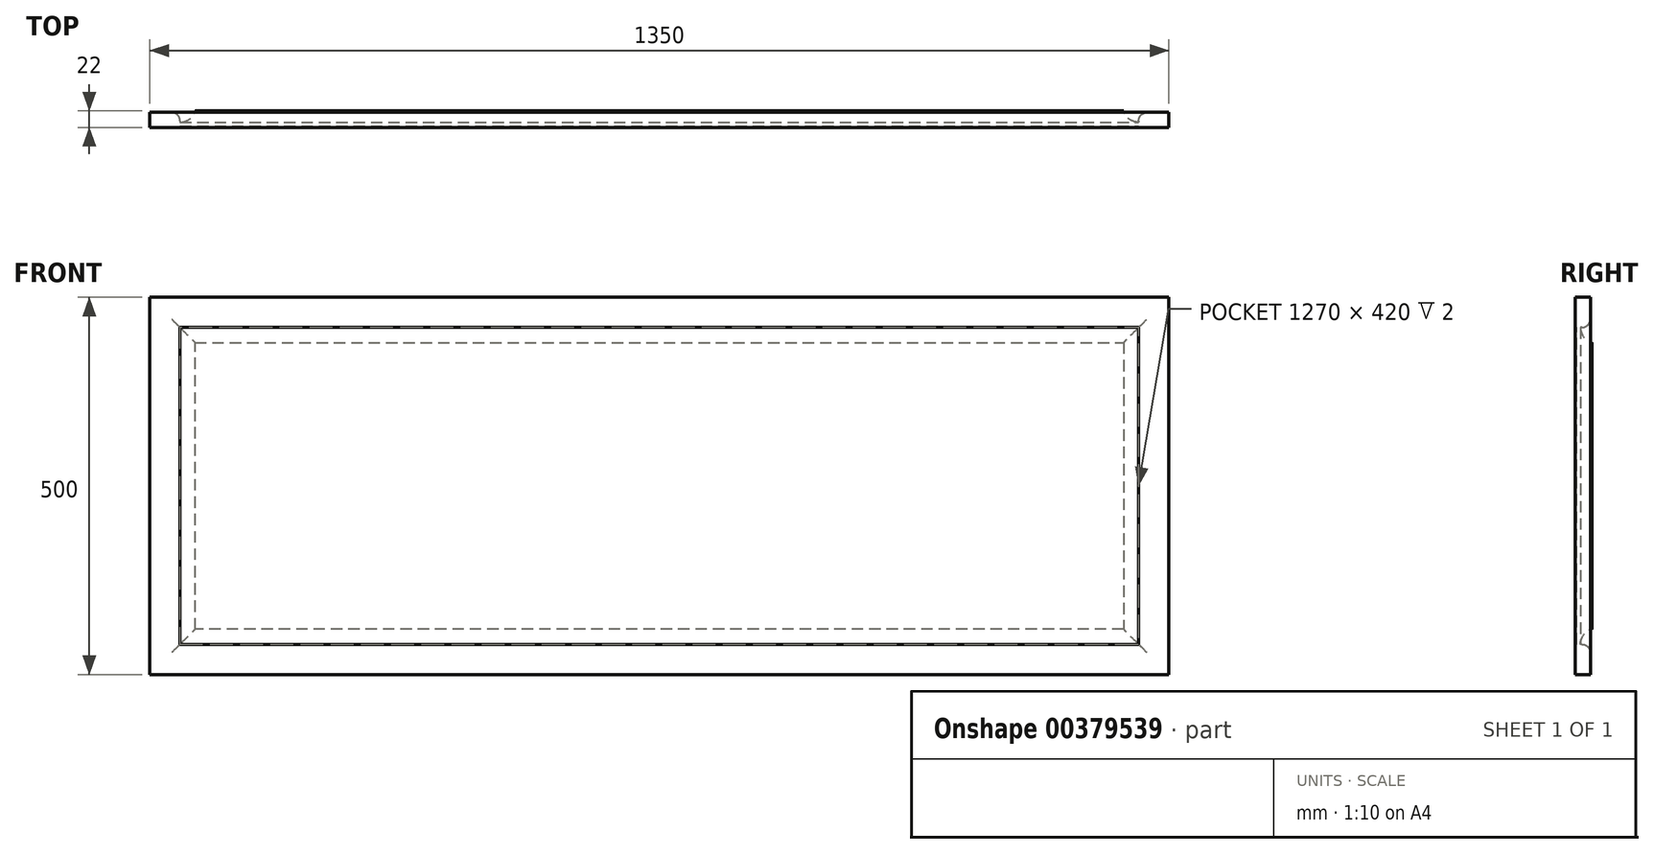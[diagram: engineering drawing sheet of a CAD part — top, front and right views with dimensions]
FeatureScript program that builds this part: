
annotation { "Feature Type Name" : "Feature", "Feature Type Description" : "" }
export const myFeature = defineFeature(function(context is Context, id is Id, definition is map)
    precondition{}
    {
        {
            var Q0;
            Q0=qCreatedBy(makeId("Front.planeOp"),FACE);
            var sketch = newSketch(context, id + "F0", { "sketchPlane" : qUnion([Q0])});
            skLineSegment(sketch, "E0.bottom", {"start": v(-675, 250) * mm, "end": v(675, 250) * mm});
            skLineSegment(sketch, "E0.top", {"start": v(-675, -250) * mm, "end": v(675, -250) * mm});
            skLineSegment(sketch, "E0.left", {"start": v(-675, 250) * mm, "end": v(-675, -250) * mm});
            skLineSegment(sketch, "E0.right", {"start": v(675, 250) * mm, "end": v(675, -250) * mm});
            skPoint(sketch, "E0.middle", {"position": v(0, 0) * mm});
            skLineSegment(sketch, "E1", {"start": v(-675, 250) * mm, "end": v(-225, 250) * mm, "construction": true});
            skLineSegment(sketch, "E2", {"start": v(-225, 250) * mm, "end": v(225, 250) * mm, "construction": true});
            skLineSegment(sketch, "E3", {"start": v(225, 250) * mm, "end": v(675, 250) * mm, "construction": true});
            skLineSegment(sketch, "E4", {"start": v(-225, 250) * mm, "end": v(-225, -250) * mm});
            skLineSegment(sketch, "E5", {"start": v(225, 250) * mm, "end": v(225, -250) * mm});
            skSolve(sketch);
        }
        {
            var Q0;
            Q0=qCreatedBy(makeId("Top.planeOp"),FACE);
            var sketch = newSketch(context, id + "F1", { "sketchPlane" : qUnion([Q0])});
            skLineSegment(sketch, "E6", {"start": v(0, 0) * mm, "end": v(-675, 0) * mm, "construction": true});
            skLineSegment(sketch, "E7", {"start": v(0, 0) * mm, "end": v(675, 0) * mm});
            skLineSegment(sketch, "E8", {"start": v(-675, 0) * mm, "end": v(-675, -7) * mm});
            skLineSegment(sketch, "E9", {"start": v(-675, -7) * mm, "end": v(-635, -7) * mm});
            skLineSegment(sketch, "E10", {"start": v(-635, -7) * mm, "end": v(-635, 0) * mm});
            skLineSegment(sketch, "E11", {"start": v(-635, 0) * mm, "end": v(-615, 0) * mm});
            skLineSegment(sketch, "E12", {"start": v(-615, 0) * mm, "end": v(-615, 15) * mm});
            skLineSegment(sketch, "E13", {"start": v(-675, 0) * mm, "end": v(-425, 0) * mm, "construction": true});
            skLineSegment(sketch, "E14", {"start": v(-615, 15) * mm, "end": v(-425, 15) * mm});
            skLineSegment(sketch, "E15", {"start": v(-425, 15) * mm, "end": v(-425, 0) * mm});
            skArc(sketch, "E16", {"start": v(-635, 0) * mm, "mid": v(-622.5, 4.17) * mm, "end": v(-615, 15) * mm});
            skLineSegment(sketch, "E17", {"start": v(-675, 0) * mm, "end": v(-675, 13) * mm});
            skLineSegment(sketch, "E18", {"start": v(-675, 13) * mm, "end": v(-646.18, 13) * mm});
            skLineSegment(sketch, "E19", {"start": v(-635, 0) * mm, "end": v(-635, 1.88) * mm});
            skArc(sketch, "E20", {"start": v(-635, 1.88) * mm, "mid": v(-638.28, 9.76) * mm, "end": v(-646.18, 13) * mm});
            skLineSegment(sketch, "E21", {"start": v(-635, -5) * mm, "end": v(-425, -5) * mm});
            skLineSegment(sketch, "E22", {"start": v(-425, -5) * mm, "end": v(-425, 0) * mm});
            skSolve(sketch);
        }
        {
            var Q0;
            {var subQ0=sQuery(id+"F1.wireOp",EDGE,"E11");Q0=makeQuery(id+"F1.imprint","IMPRINT",FACE,{"disambiguationData":[TD([[makeQuery(id+"F1.imprint","IMPRINT",EDGE,{"derivedFrom":subQ0}),-1.0]])]});}
            var Q1;
            Q1=makeQuery(id+"F1.imprint","IMPRINT",FACE,{"disambiguationData":[TD([[makeQuery(id+"F1.imprint","IMPRINT",EDGE,{"derivedFrom":sQuery(id+"F1.wireOp",EDGE,"E11")}),1.0]])]});
            var Q2;
            Q2=makeQuery(id+"F1.imprint","IMPRINT",FACE,{"disambiguationData":[TD([[makeQuery(id+"F1.imprint","IMPRINT",EDGE,{"derivedFrom":sQuery(id+"F1.wireOp",EDGE,"E8")}),1.0]])]});
            var Q3;
            Q3=sQuery(id+"F0.wireOp",EDGE,"E0.left");
            var Q4;
            Q4=sQuery(id+"F0.wireOp",EDGE,"E0.bottom");
            var Q5;
            Q5=sQuery(id+"F0.wireOp",EDGE,"E0.right");
            var Q6;
            Q6=sQuery(id+"F0.wireOp",EDGE,"E0.top");
            sweep(context, id + "F2", {"profiles" : qUnion([Q0, Q1, Q2]), "path" : qUnion([Q3, Q4, Q5, Q6])});
        }
    });
